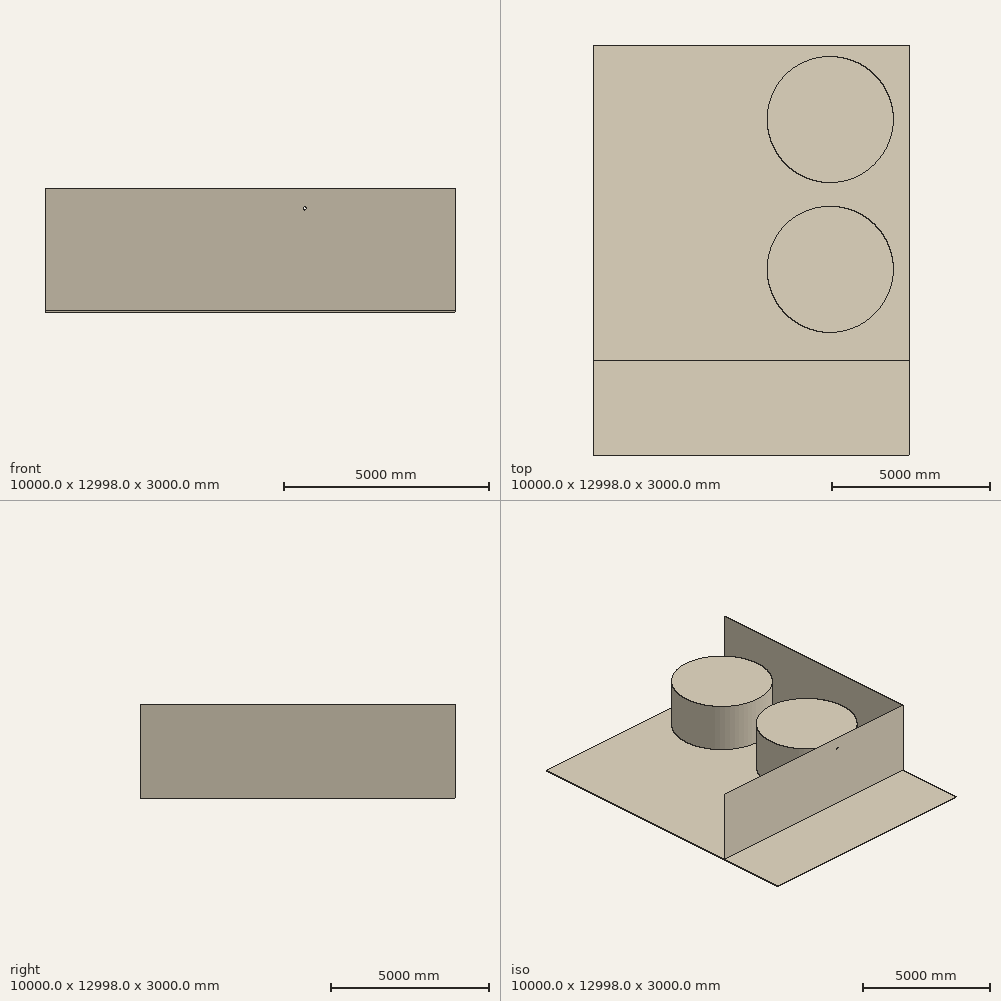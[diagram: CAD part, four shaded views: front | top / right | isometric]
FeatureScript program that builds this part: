
annotation { "Feature Type Name" : "Feature", "Feature Type Description" : "" }
export const myFeature = defineFeature(function(context is Context, id is Id, definition is map)
    precondition{}
    {
        {
            var Q0;
            Q0=qCreatedBy(makeId("Top.planeOp"),FACE);
            var sketch = newSketch(context, id + "F0", { "sketchPlane" : qUnion([Q0])});
            skLineSegment(sketch, "E0.bottom", {"start": v(-5000, 5000) * mm, "end": v(5000, 5000) * mm});
            skLineSegment(sketch, "E0.top", {"start": v(-5000, -5000) * mm, "end": v(5000, -5000) * mm});
            skLineSegment(sketch, "E0.left", {"start": v(-5000, 5000) * mm, "end": v(-5000, -5000) * mm});
            skLineSegment(sketch, "E0.right", {"start": v(5000, 5000) * mm, "end": v(5000, -5000) * mm});
            skPoint(sketch, "E0.middle", {"position": v(0, 0) * mm});
            skLineSegment(sketch, "E1", {"start": v(-5000, -4998) * mm, "end": v(4998, -4998) * mm});
            skLineSegment(sketch, "E2", {"start": v(4998, 5000) * mm, "end": v(4998, -4998) * mm});
            skCircle(sketch, "E3", {"center": v(2498, 2652) * mm, "radius": 2000 * mm});
            skCircle(sketch, "E4", {"center": v(2498, -2098) * mm, "radius": 2000 * mm});
            skLineSegment(sketch, "E5.top", {"start": v(-5000, -7998) * mm, "end": v(5000, -7998) * mm});
            skLineSegment(sketch, "E5.left", {"start": v(-5000, -4998) * mm, "end": v(-5000, -7998) * mm});
            skLineSegment(sketch, "E5.right", {"start": v(5000, -4998) * mm, "end": v(5000, -7998) * mm});
            skSolve(sketch);
        }
        {
            var Q0;
            {var subQ2=sQuery(id+"F0.wireOp",EDGE,"E0.top");Q0=makeQuery(id+"F0.imprint","IMPRINT",FACE,{"disambiguationData":[TD([[makeQuery(id+"F0.imprint","IMPRINT",EDGE,{"derivedFrom":subQ2}),1.0]])]});}
            extrude(context, id + "F1", {"entities" : qUnion([Q0]), "depth" : 3000 * mm, "offsetDistance" : 25 * mm});
        }
        {
            var Q0;
            {var subQ4=sQuery(id+"F0.wireOp",EDGE,"E1");Q0=makeQuery(id+"F0.imprint","IMPRINT",FACE,{"disambiguationData":[TD([[makeQuery(id+"F0.imprint","IMPRINT",EDGE,{"derivedFrom":subQ4}),1.0]])]});}
            var Q1;
            Q1=makeQuery(id+"F0.imprint","IMPRINT",FACE,{"disambiguationData":[TD([[makeQuery(id+"F0.imprint","IMPRINT",EDGE,{"derivedFrom":sQuery(id+"F0.wireOp",EDGE,"E3")}),1.0]])]});
            var Q2;
            Q2=makeQuery(id+"F0.imprint","IMPRINT",FACE,{"disambiguationData":[TD([[makeQuery(id+"F0.imprint","IMPRINT",EDGE,{"derivedFrom":sQuery(id+"F0.wireOp",EDGE,"E4")}),1.0]])]});
            var Q3;
            {var subQ1=sQuery(id+"F0.wireOp",EDGE,"E0.left");Q3=makeQuery(id+"F0.imprint","IMPRINT",FACE,{"disambiguationData":[TD([[makeQuery(id+"F0.imprint","IMPRINT",EDGE,{"derivedFrom":subQ1}),1.0]])]});}
            var Q4;
            {var subQ5=sQuery(id+"F0.wireOp",EDGE,"E5.top");Q4=makeQuery(id+"F0.imprint","IMPRINT",FACE,{"disambiguationData":[TD([[makeQuery(id+"F0.imprint","IMPRINT",EDGE,{"derivedFrom":subQ5}),1.0]])]});}
            extrude(context, id + "F2", {"entities" : qUnion([Q0, Q1, Q2, Q3, Q4]), "operationType" : NewBodyOperationType.ADD, "depth" : 25 * mm, "offsetDistance" : 25 * mm});
        }
        {
            var Q0;
            Q0=makeQuery(id+"F0.imprint","IMPRINT",FACE,{"disambiguationData":[TD([[makeQuery(id+"F0.imprint","IMPRINT",EDGE,{"derivedFrom":sQuery(id+"F0.wireOp",EDGE,"E3")}),1.0]])]});
            var Q1;
            Q1=makeQuery(id+"F0.imprint","IMPRINT",FACE,{"disambiguationData":[TD([[makeQuery(id+"F0.imprint","IMPRINT",EDGE,{"derivedFrom":sQuery(id+"F0.wireOp",EDGE,"E4")}),1.0]])]});
            extrude(context, id + "F3", {"entities" : qUnion([Q0, Q1]), "depth" : 2000 * mm, "offsetDistance" : 25 * mm});
        }
        {
            var Q0;
            Q0=makeQuery(id+"F1.opExtrude","SWEPT_FACE",FACE,{"disambiguationData":[OSD([sQuery(id+"F0.wireOp",EDGE,"E0.top")])]});
            var sketch = newSketch(context, id + "F4", { "sketchPlane" : qUnion([Q0])});
            skLineSegment(sketch, "E6", {"start": v(5000, 25) * mm, "end": v(1330, 25) * mm, "construction": true});
            skLineSegment(sketch, "E7", {"start": v(1330, 25) * mm, "end": v(1330, 175) * mm, "construction": true});
            skPoint(sketch, "E8", {"position": v(1330, 175) * mm});
            skPoint(sketch, "E9", {"position": v(1330, 25) * mm});
            skLineSegment(sketch, "E10", {"start": v(1330, 175) * mm, "end": v(1330, 2525) * mm, "construction": true});
            skPoint(sketch, "E11", {"position": v(1330, 2525) * mm});
            skSolve(sketch);
        }
        {
            var Q0;
            Q0=sQuery(id+"F4.wireOp",VERTEX,"E11");
            var Q1;
            Q1=makeQuery(id+"F1.opExtrude","SWEPT_BODY",BODY,{"disambiguationData":[OSD([sQuery(id+"F0.wireOp",EDGE,"E0.bottom"),sQuery(id+"F0.wireOp",EDGE,"E0.top"),sQuery(id+"F0.wireOp",EDGE,"E0.right"),sQuery(id+"F0.wireOp",EDGE,"E2"),sQuery(id+"F0.wireOp",EDGE,"E1"),sQuery(id+"F0.wireOp",EDGE,"E5.left"),sQuery(id+"F0.wireOp",EDGE,"E5.right")])]});
            hole(context, id + "F5", {"style" : HoleStyle.SIMPLE, "endStyle" : HoleEndStyle.BLIND, "holeDiameter" : 75 * mm, "majorDiameter" : 5 * mm, "holeDepth" : 100 * mm, "isTappedThrough" : true, "tappedDepth" : 12 * mm, "tapClearance" : 3, "startFromSketch" : true, "locations" : qUnion([Q0]), "scope" : qUnion([Q1])});
        }
    });
